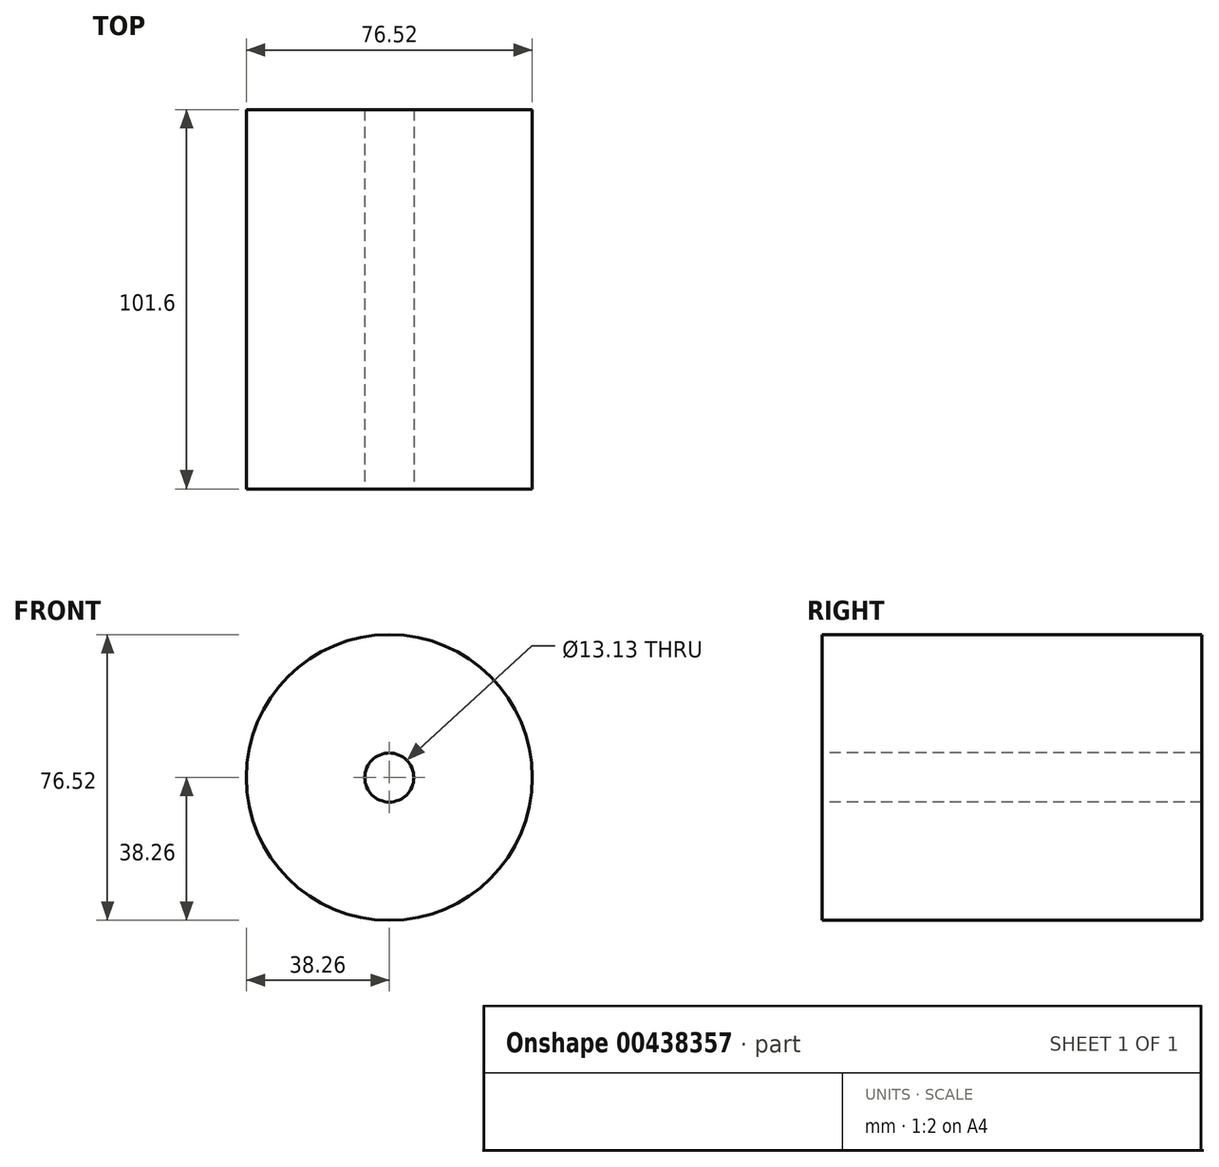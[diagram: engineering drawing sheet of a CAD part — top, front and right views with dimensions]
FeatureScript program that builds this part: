
annotation { "Feature Type Name" : "Feature", "Feature Type Description" : "" }
export const myFeature = defineFeature(function(context is Context, id is Id, definition is map)
    precondition{}
    {
        {
            var Q0;
            Q0=qCreatedBy(makeId("Front.planeOp"),FACE);
            var sketch = newSketch(context, id + "F0", { "sketchPlane" : qUnion([Q0])});
            skCircle(sketch, "E0", {"center": v(0, 0) * mm, "radius": 38.26 * mm});
            skSolve(sketch);
        }
        {
            var Q0;
            Q0=makeQuery(id+"F0.imprint","IMPRINT",FACE,{"disambiguationData":[TD([[makeQuery(id+"F0.imprint","IMPRINT",EDGE,{"derivedFrom":sQuery(id+"F0.wireOp",EDGE,"E0")}),1.0]])]});
            extrude(context, id + "F1", {"entities" : qUnion([Q0]), "depth" : 101.6 * mm});
        }
        {
            var Q0;
            Q0=makeQuery(id+"F1.opExtrude","CAP_FACE",FACE,{"disambiguationData":[OSD([sQuery(id+"F0.wireOp",EDGE,"E0")])],"isStart":false});
            var sketch = newSketch(context, id + "F2", { "sketchPlane" : qUnion([Q0])});
            skCircle(sketch, "E1", {"center": v(0, 0) * mm, "radius": 6.56 * mm});
            skSolve(sketch);
        }
        {
            var Q0;
            Q0=makeQuery(id+"F2.imprint","IMPRINT",FACE,{"disambiguationData":[TD([[makeQuery(id+"F2.imprint","IMPRINT",EDGE,{"derivedFrom":sQuery(id+"F2.wireOp",EDGE,"E1")}),1.0]])]});
            var Q1;
            Q1=sQuery(id+"F2.wireOp",EDGE,"E1");
            extrude(context, id + "F3", {"entities" : qUnion([Q0]), "operationType" : NewBodyOperationType.REMOVE, "surfaceEntities" : qUnion([Q1]), "oppositeDirection" : true, "depth" : 105.92 * mm});
        }
    });
